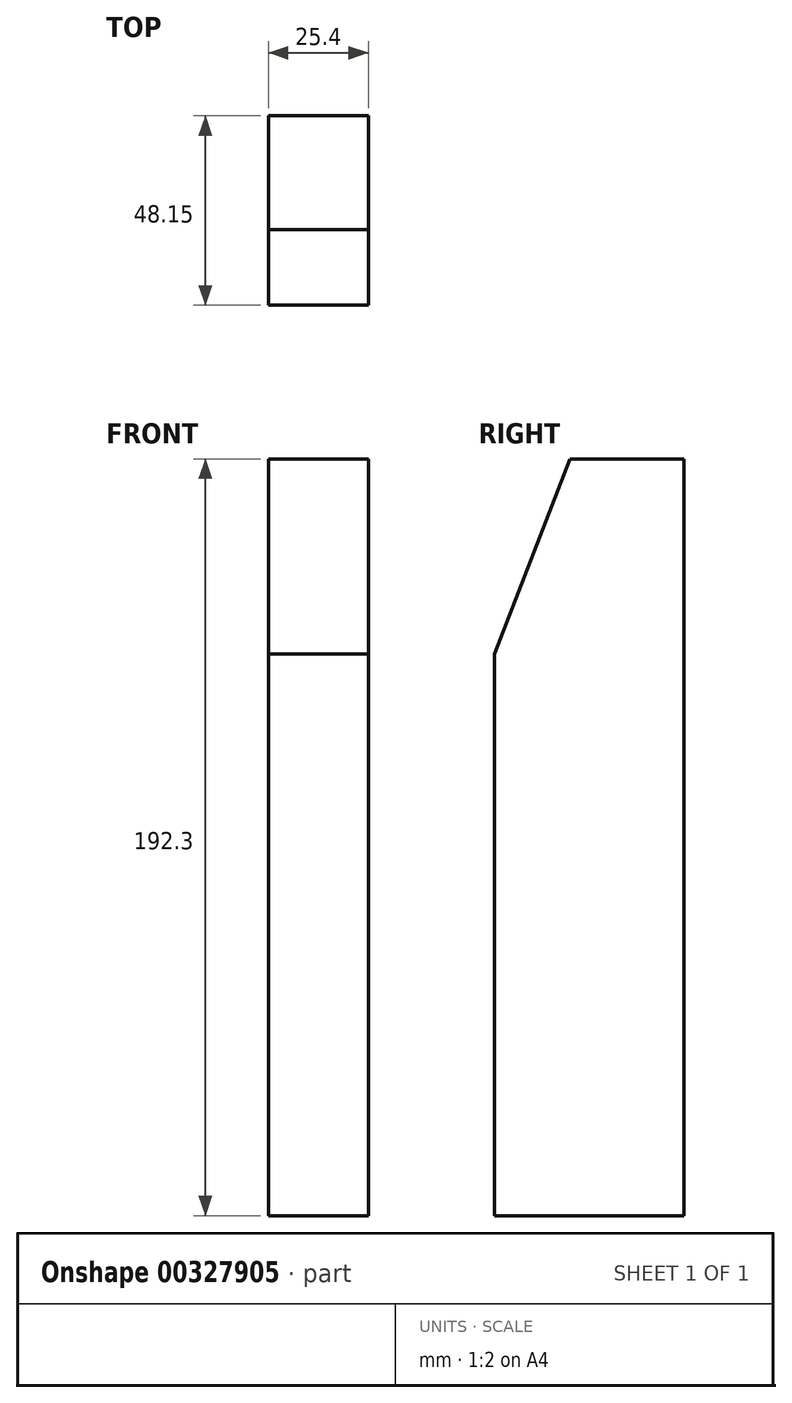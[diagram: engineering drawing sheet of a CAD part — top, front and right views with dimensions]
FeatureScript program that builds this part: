
annotation { "Feature Type Name" : "Feature", "Feature Type Description" : "" }
export const myFeature = defineFeature(function(context is Context, id is Id, definition is map)
    precondition{}
    {
        {
            var Q0;
            Q0=qCreatedBy(makeId("Right.planeOp"),FACE);
            var sketch = newSketch(context, id + "F0", { "sketchPlane" : qUnion([Q0])});
            skLineSegment(sketch, "E0", {"start": v(0, 175.11) * mm, "end": v(-28.94, 175.11) * mm});
            skLineSegment(sketch, "E1", {"start": v(-28.94, 175.11) * mm, "end": v(-48.15, 125.47) * mm});
            skLineSegment(sketch, "E2", {"start": v(-48.15, 125.47) * mm, "end": v(-48.15, -17.2) * mm});
            skLineSegment(sketch, "E3", {"start": v(-48.15, -17.2) * mm, "end": v(0, -17.2) * mm});
            skLineSegment(sketch, "E4", {"start": v(0, -17.2) * mm, "end": v(0, 175.11) * mm});
            skSolve(sketch);
        }
        {
            var Q0;
            Q0=makeQuery(id+"F0.imprint","IMPRINT",FACE,{"disambiguationData":[TD([[makeQuery(id+"F0.imprint","IMPRINT",EDGE,{"derivedFrom":sQuery(id+"F0.wireOp",EDGE,"E0")}),1.0]])]});
            extrude(context, id + "F1", {"entities" : qUnion([Q0]), "endBound" : BoundingType.SYMMETRIC, "depth" : 25.4 * mm});
        }
    });
